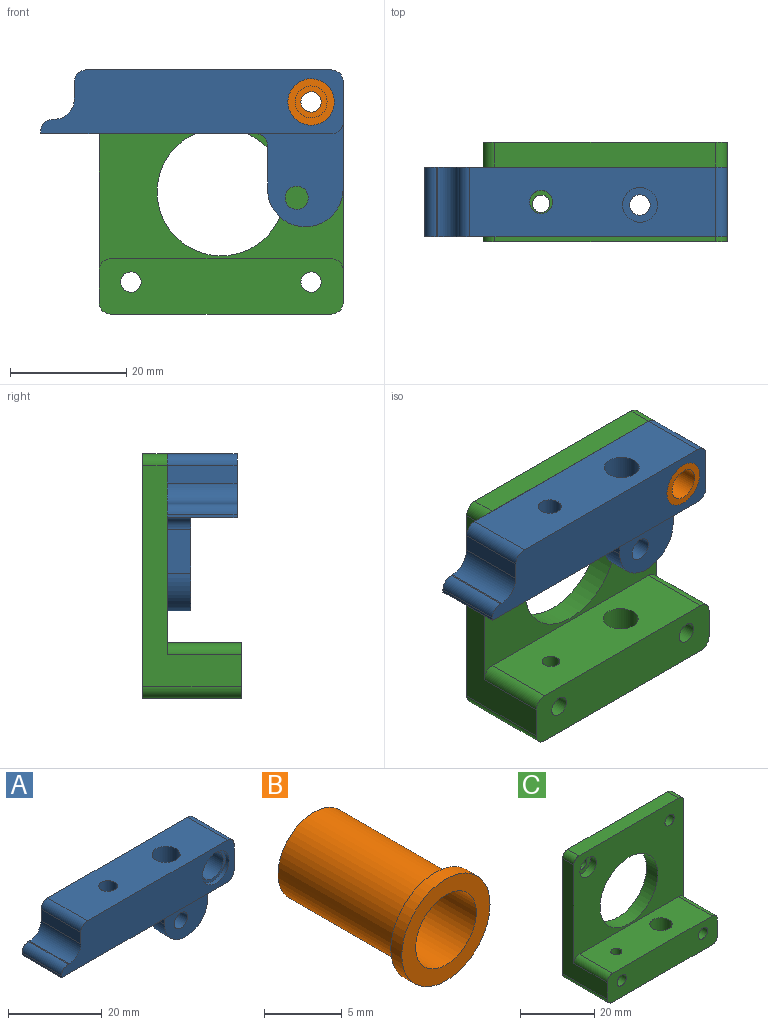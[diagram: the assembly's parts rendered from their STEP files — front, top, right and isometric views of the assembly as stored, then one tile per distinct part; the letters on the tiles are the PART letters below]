
ASSEMBLY  parts=3 mates=2
PART A: 25 faces, bbox 52x12x27 mm
  f0: plane 42.25x12mm, normal (0,0,1), area 466.2mm2, adj f8,f9,f18,f19,f22,f23
  f1: plane 50x12mm, normal (0,0,-1), area 525.8mm2, adj f7,f8,f9,f15,f16,f17,f21,f22
  f2: plane 18.5x12mm, normal (1,0,0), area 130mm2, adj f8,f9,f13,f15,f17,f18
  f3: plane 12x3mm, normal (-1,0,0), area 36mm2, adj f4,f8,f9,f19
  f4: cylinder r=3.5mm len=12mm, axis (0,1,0), area 66mm2, adj f3,f5,f8,f9
  f5: plane 12x0.25mm, normal (0,0,1), area 3mm2, adj f4,f8,f9,f20
  f6: cylinder r=4mm len=8mm, axis (0,1,0), area 25.1mm2, adj f8,f11
  f7: plane 12x0.5mm, normal (-1,0,0), area 6mm2, adj f1,f8,f9,f20
  f8: plane 52x11mm, normal (0,-1,0), area 472.1mm2, adj f0,f1,f2,f3,f4,f5,f6,f7
  f9: plane 52x27mm, normal (0,1,0), area 668.2mm2, adj f0,f1,f2,f3,f4,f5,f7,f10
  f10: cylinder r=3.25mm len=11mm, axis (0,1,0), area 224.6mm2, adj f9,f11
  f11: plane 8x8mm, normal (0,-1,0), area 17.1mm2, adj f6,f10
  f12: plane 7.5x4mm, normal (-1,0,0), area 30mm2, adj f9,f13,f15,f16
  f13: cylinder r=6.5mm len=13mm, axis (0,1,0), area 81.7mm2, adj f2,f9,f12,f15
  f14: cylinder r=2mm len=4mm, axis (0,1,0), area 50.3mm2, adj f9,f15
  f15: plane 18x15mm, normal (0,-1,0), area 179mm2, adj f1,f2,f12,f13,f14,f16,f17
  f16: cylinder r=2mm len=4mm, axis (0,-1,0), area 12.6mm2, adj f1,f9,f12,f15
  f17: cylinder r=2mm len=8mm, axis (0,1,0), area 25.1mm2, adj f1,f2,f8,f15
  f18: cylinder r=2mm len=12mm, axis (0,1,0), area 37.7mm2, adj f0,f2,f8,f9
  f19: cylinder r=2mm len=12mm, axis (0,-1,0), area 37.7mm2, adj f0,f3,f8,f9
  f20: cylinder r=2mm len=12mm, axis (0,1,0), area 37.7mm2, adj f5,f7,f8,f9
  f21: cylinder r=1.75mm len=3.5mm, axis (0,0,1), area 11mm2, adj f1,f24
  f22: cylinder r=2mm len=11mm, axis (0,0,1), area 138.2mm2, adj f0,f1
  f23: cylinder r=3mm len=10mm, axis (0,0,1), area 188.5mm2, adj f0,f24
  f24: plane 6x6mm, normal (0,0,1), area 18.7mm2, adj f21,f23
PART B: 8 faces, bbox 8x12x8 mm
  f0: cylinder r=4mm len=8mm, axis (0,-1,0), area 25.1mm2, adj f1,f2
  f1: plane 8x8mm, normal (0,1,0), area 17.1mm2, adj f0,f3
  f2: plane 8x8mm, normal (0,-1,0), area 26.5mm2, adj f0,f6
  f3: cylinder r=3.25mm len=11mm, axis (0,-1,0), area 224.6mm2, adj f1,f5
  f4: cylinder r=1.75mm len=7mm, axis (0,-1,0), area 77mm2, adj f5,f7
  f5: plane 6.5x6.5mm, normal (0,1,0), area 23.6mm2, adj f3,f4
  f6: cylinder r=2.75mm len=5.5mm, axis (0,-1,0), area 86.4mm2, adj f2,f7
  f7: plane 5.5x5.5mm, normal (0,-1,0), area 14.1mm2, adj f4,f6
PART C: 23 faces, bbox 42x17x42 mm
  f0: plane 38x17mm, normal (1,0,0), area 231.6mm2, adj f6,f7,f12,f19,f20,f21
  f1: plane 38x4.25mm, normal (0,0,1), area 161.5mm2, adj f6,f7,f21,f22
  f2: plane 38x17mm, normal (-1,0,0), area 231.6mm2, adj f6,f7,f12,f17,f18,f22
  f3: cylinder r=11mm len=22mm, axis (0,1,0), area 293.7mm2, adj f6,f7
  f4: cylinder r=1.75mm len=4.25mm, axis (0,1,0), area 46.7mm2, adj f6,f7
  f5: cylinder r=3.12mm len=6.25mm, axis (0,1,0), area 44.2mm2, adj f6,f14
  f6: plane 42x34.5mm, normal (0,-1,0), area 944.6mm2, adj f0,f1,f2,f3,f4,f5,f8,f17
  f7: plane 42x42mm, normal (0,1,0), area 1341.9mm2, adj f0,f1,f2,f3,f4,f9,f10,f11
  f8: plane 38x12.75mm, normal (0,0,1), area 449.2mm2, adj f6,f12,f15,f16,f17,f20
  f9: plane 38x17mm, normal (0,0,-1), area 610.7mm2, adj f7,f12,f15,f16,f18,f19
  f10: cylinder r=1.75mm len=17mm, axis (0,1,0), area 186.9mm2, adj f7,f12
  f11: cylinder r=1.75mm len=17mm, axis (0,1,0), area 186.9mm2, adj f7,f12
  f12: plane 42x9.5mm, normal (0,-1,0), area 376.3mm2, adj f0,f2,f8,f9,f10,f11,f17,f18
  f13: cylinder r=1.75mm len=3.5mm, axis (0,1,0), area 22mm2, adj f7,f14
  f14: plane 6.25x6.25mm, normal (0,-1,0), area 21.1mm2, adj f5,f13
  f15: cylinder r=1.5mm len=9.5mm, axis (0,0,-1), area 89.5mm2, adj f8,f9
  f16: cylinder r=3mm len=9.5mm, axis (0,0,-1), area 179.1mm2, adj f8,f9
  f17: cylinder r=2mm len=12.75mm, axis (0,1,0), area 40.1mm2, adj f2,f6,f8,f12
  f18: cylinder r=2mm len=17mm, axis (0,1,0), area 53.4mm2, adj f2,f7,f9,f12
  f19: cylinder r=2mm len=17mm, axis (0,-1,0), area 53.4mm2, adj f0,f7,f9,f12
  f20: cylinder r=2mm len=12.75mm, axis (0,-1,0), area 40.1mm2, adj f0,f6,f8,f12
  f21: cylinder r=2mm len=4.25mm, axis (0,1,0), area 13.4mm2, adj f0,f1,f6,f7
  f22: cylinder r=2mm len=4.25mm, axis (0,-1,0), area 13.4mm2, adj f1,f2,f6,f7
PLACE A t=(-18.11,1.99,0.13)mm
PLACE B t=(-18.11,1.99,0.13)mm
PLACE C t=(-18.11,1.99,0.13)mm
MATE revolute B.f0 <-> A.f6  axis (0,-1,0) through (-2.61,-14.26,15.63)mm
MATE fastened B.f0 <-> C.f4  axis (0,1,0) through (-2.61,-2.26,15.63)mm
